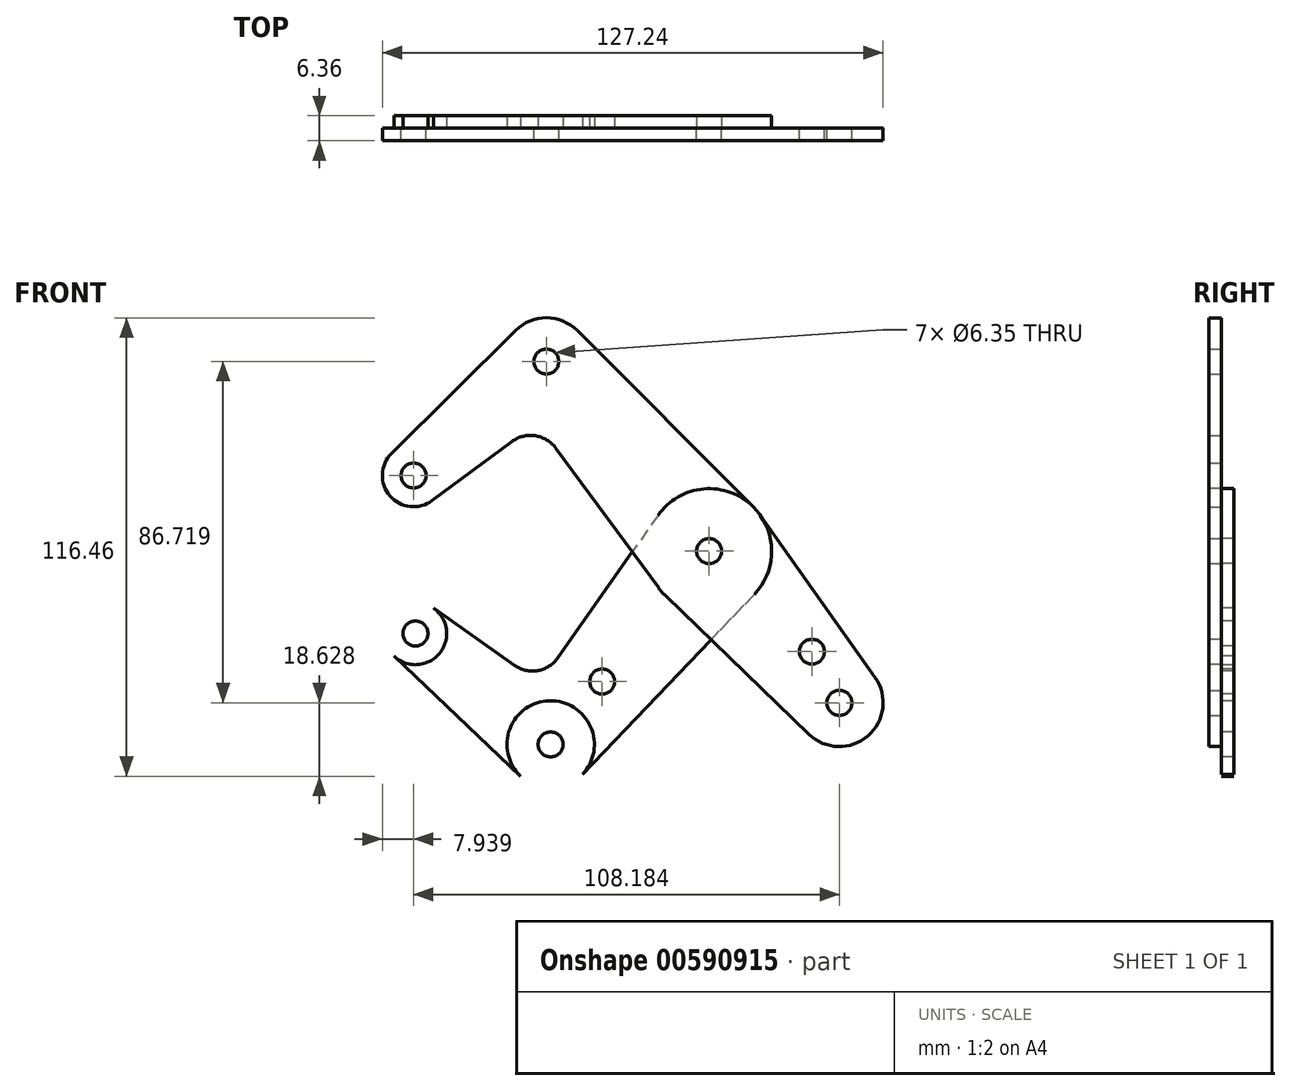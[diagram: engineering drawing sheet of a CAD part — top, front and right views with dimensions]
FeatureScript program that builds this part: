
annotation { "Feature Type Name" : "Feature", "Feature Type Description" : "" }
export const myFeature = defineFeature(function(context is Context, id is Id, definition is map)
    precondition{}
    {
        {
            var Q0;
            Q0=qCreatedBy(makeId("Front.planeOp"),FACE);
            var sketch = newSketch(context, id + "F0", { "sketchPlane" : qUnion([Q0])});
            skCircle(sketch, "E0", {"center": v(0, 0) * mm, "radius": 15.88 * mm});
            skCircle(sketch, "E1", {"center": v(-41.37, 48.18) * mm, "radius": 11.11 * mm});
            skCircle(sketch, "E2", {"center": v(-75.1, 19.22) * mm, "radius": 7.94 * mm});
            skCircle(sketch, "E3", {"center": v(33.1, -38.54) * mm, "radius": 11.11 * mm});
            skCircle(sketch, "E4", {"center": v(26.11, -25.54) * mm, "radius": 3.18 * mm});
            skCircle(sketch, "E5", {"center": v(-75.1, 19.22) * mm, "radius": 3.18 * mm});
            skCircle(sketch, "E6", {"center": v(-41.37, 48.18) * mm, "radius": 3.18 * mm});
            skCircle(sketch, "E7", {"center": v(0, 0) * mm, "radius": 3.98 * mm});
            skCircle(sketch, "E8", {"center": v(33.1, -38.54) * mm, "radius": 3.18 * mm});
            skLineSegment(sketch, "E9", {"start": v(-41.37, 48.18) * mm, "end": v(-75.1, 19.22) * mm, "construction": true});
            skCircle(sketch, "E10", {"center": v(0, 0) * mm, "radius": 3.18 * mm});
            skLineSegment(sketch, "E11", {"start": v(12.96, 9.17) * mm, "end": v(42.17, -32.12) * mm});
            skLineSegment(sketch, "E12", {"start": v(-80.68, 24.86) * mm, "end": v(-49.19, 56.07) * mm});
            skLineSegment(sketch, "E13", {"start": v(25.38, -46.54) * mm, "end": v(-11.02, -11.43) * mm});
            skLineSegment(sketch, "E14", {"start": v(-33.5, 56.03) * mm, "end": v(11.23, 11.22) * mm});
            skLineSegment(sketch, "E15", {"start": v(-12.79, -9.4) * mm, "end": v(-38.98, 26.18) * mm});
            skLineSegment(sketch, "E16", {"start": v(-70.36, 12.84) * mm, "end": v(-50.12, 27.86) * mm});
            skArc(sketch, "E17.filletArc", {"start": v(-38.98, 26.18) * mm, "mid": v(-44.2, 29.33) * mm, "end": v(-50.12, 27.86) * mm});
            skCircle(sketch, "E18.MirrorC", {"center": v(-40.26, -49.1) * mm, "radius": 3.18 * mm});
            skCircle(sketch, "E19.MirrorC", {"center": v(-74.63, -20.92) * mm, "radius": 3.18 * mm});
            skCircle(sketch, "E20.MirrorC", {"center": v(-74.63, -20.92) * mm, "radius": 7.94 * mm});
            skLineSegment(sketch, "E21.MirrorCS", {"start": v(-32.22, -56.77) * mm, "end": v(11.49, -10.96) * mm});
            skCircle(sketch, "E22.MirrorC", {"center": v(-40.26, -49.1) * mm, "radius": 11.11 * mm});
            skLineSegment(sketch, "E23.MirrorCS", {"start": v(-40.26, -49.1) * mm, "end": v(-74.63, -20.92) * mm, "construction": true});
            skLineSegment(sketch, "E24.MirrorCS", {"start": v(-70.05, -14.44) * mm, "end": v(-49.47, -28.99) * mm});
            skLineSegment(sketch, "E25.MirrorCS", {"start": v(-80.1, -26.68) * mm, "end": v(-47.9, -57.17) * mm});
            skLineSegment(sketch, "E26", {"start": v(-13, 9.12) * mm, "end": v(-38.37, -27.06) * mm});
            skArc(sketch, "E27.filletArc", {"start": v(-49.47, -28.99) * mm, "mid": v(-43.52, -30.33) * mm, "end": v(-38.37, -27.06) * mm});
            skLineSegment(sketch, "E28", {"start": v(0, 0) * mm, "end": v(-40.26, -49.1) * mm, "construction": true});
            skLineSegment(sketch, "E29", {"start": v(-40.26, -49.1) * mm, "end": v(-27.17, -33.14) * mm});
            skCircle(sketch, "E30", {"center": v(-27.17, -33.14) * mm, "radius": 3.18 * mm});
            skLineSegment(sketch, "E31", {"start": v(-41.37, 48.18) * mm, "end": v(0, 0) * mm, "construction": true});
            skLineSegment(sketch, "E32", {"start": v(0, 0) * mm, "end": v(33.1, -38.54) * mm, "construction": true});
            skSolve(sketch);
        }
        {
            var Q0;
            {var subQ0=sQuery(id+"F0.wireOp",EDGE,"E12");Q0=makeQuery(id+"F0.imprint","IMPRINT",FACE,{"disambiguationData":[TD([[makeQuery(id+"F0.imprint","IMPRINT",EDGE,{"derivedFrom":subQ0}),-1.0]])]});}
            var Q1;
            Q1=makeQuery(id+"F0.imprint","IMPRINT",FACE,{"disambiguationData":[TD([[makeQuery(id+"F0.imprint","IMPRINT",EDGE,{"derivedFrom":sQuery(id+"F0.wireOp",EDGE,"E6")}),-1.0]])]});
            var Q2;
            Q2=makeQuery(id+"F0.imprint","IMPRINT",FACE,{"disambiguationData":[TD([[makeQuery(id+"F0.imprint","IMPRINT",EDGE,{"derivedFrom":sQuery(id+"F0.wireOp",EDGE,"E4")}),-1.0]])]});
            var Q3;
            {var subQ0=sQuery(id+"F0.wireOp",EDGE,"E15");var subQ1=sQuery(id+"F0.wireOp",EDGE,"E0");var subQ2=makeQuery(id+"F0.imprint","INTERSECT",VERTEX,{"derivedFrom":[subQ1,subQ0]});Q3=makeQuery(id+"F0.imprint","IMPRINT",FACE,{"disambiguationData":[TD([[makeQuery(id+"F0.imprint","IMPRINT",EDGE,{"disambiguationData":[TD([[subQ2,1.0]])],"derivedFrom":subQ1}),-1.0]])]});}
            var Q4;
            {var subQ0=sQuery(id+"F0.wireOp",EDGE,"E13");var subQ1=sQuery(id+"F0.wireOp",EDGE,"E0");var subQ2=makeQuery(id+"F0.imprint","INTERSECT",VERTEX,{"derivedFrom":[subQ1,subQ0]});Q4=makeQuery(id+"F0.imprint","IMPRINT",FACE,{"disambiguationData":[TD([[makeQuery(id+"F0.imprint","IMPRINT",EDGE,{"disambiguationData":[TD([[subQ2,-1.0]])],"derivedFrom":subQ1}),-1.0]])]});}
            var Q5;
            Q5=makeQuery(id+"F0.imprint","IMPRINT",FACE,{"disambiguationData":[TD([[makeQuery(id+"F0.imprint","IMPRINT",EDGE,{"derivedFrom":sQuery(id+"F0.wireOp",EDGE,"E8")}),-1.0]])]});
            var Q6;
            Q6=makeQuery(id+"F0.imprint","IMPRINT",FACE,{"disambiguationData":[TD([[makeQuery(id+"F0.imprint","IMPRINT",EDGE,{"derivedFrom":sQuery(id+"F0.wireOp",EDGE,"E5")}),-1.0]])]});
            var Q7;
            Q7=makeQuery(id+"F0.imprint","IMPRINT",FACE,{"disambiguationData":[TD([[makeQuery(id+"F0.imprint","IMPRINT",EDGE,{"derivedFrom":sQuery(id+"F0.wireOp",EDGE,"E7")}),-1.0]])]});
            var Q8;
            Q8=makeQuery(id+"F0.imprint","IMPRINT",FACE,{"disambiguationData":[TD([[makeQuery(id+"F0.imprint","IMPRINT",EDGE,{"derivedFrom":sQuery(id+"F0.wireOp",EDGE,"E7")}),1.0]])]});
            extrude(context, id + "F1", {"entities" : qUnion([Q0, Q1, Q2, Q3, Q4, Q5, Q6, Q7, Q8]), "depth" : 3.17 * mm, "offsetDistance" : 25.4 * mm});
        }
        {
            var Q0;
            Q0=makeQuery(id+"F0.imprint","IMPRINT",FACE,{"disambiguationData":[TD([[makeQuery(id+"F0.imprint","IMPRINT",EDGE,{"derivedFrom":sQuery(id+"F0.wireOp",EDGE,"E19.MirrorC")}),1.0]])]});
            var Q1;
            Q1=makeQuery(id+"F0.imprint","IMPRINT",FACE,{"disambiguationData":[TD([[makeQuery(id+"F0.imprint","IMPRINT",EDGE,{"derivedFrom":sQuery(id+"F0.wireOp",EDGE,"E18.MirrorC")}),1.0]])]});
            var Q2;
            Q2=makeQuery(id+"F0.imprint","IMPRINT",FACE,{"disambiguationData":[TD([[makeQuery(id+"F0.imprint","IMPRINT",EDGE,{"derivedFrom":sQuery(id+"F0.wireOp",EDGE,"E7")}),-1.0]])]});
            var Q3;
            {var subQ11=sQuery(id+"F0.wireOp",EDGE,"E24.MirrorCS");Q3=makeQuery(id+"F0.imprint","IMPRINT",FACE,{"disambiguationData":[TD([[makeQuery(id+"F0.imprint","IMPRINT",EDGE,{"derivedFrom":subQ11}),-1.0]])]});}
            var Q4;
            {var subQ0=sQuery(id+"F0.wireOp",EDGE,"E13");var subQ1=sQuery(id+"F0.wireOp",EDGE,"E0");var subQ2=makeQuery(id+"F0.imprint","INTERSECT",VERTEX,{"derivedFrom":[subQ1,subQ0]});Q4=makeQuery(id+"F0.imprint","IMPRINT",FACE,{"disambiguationData":[TD([[makeQuery(id+"F0.imprint","IMPRINT",EDGE,{"disambiguationData":[TD([[subQ2,-1.0]])],"derivedFrom":subQ1}),-1.0]])]});}
            var Q5;
            {var subQ0=sQuery(id+"F0.wireOp",EDGE,"E15");var subQ1=sQuery(id+"F0.wireOp",EDGE,"E0");var subQ2=makeQuery(id+"F0.imprint","INTERSECT",VERTEX,{"derivedFrom":[subQ1,subQ0]});Q5=makeQuery(id+"F0.imprint","IMPRINT",FACE,{"disambiguationData":[TD([[makeQuery(id+"F0.imprint","IMPRINT",EDGE,{"disambiguationData":[TD([[subQ2,1.0]])],"derivedFrom":subQ1}),-1.0]])]});}
            var Q6;
            Q6=makeQuery(id+"F0.imprint","IMPRINT",FACE,{"disambiguationData":[TD([[makeQuery(id+"F0.imprint","IMPRINT",EDGE,{"derivedFrom":sQuery(id+"F0.wireOp",EDGE,"E7")}),1.0]])]});
            extrude(context, id + "F2", {"entities" : qUnion([Q0, Q1, Q2, Q3, Q4, Q5, Q6]), "oppositeDirection" : true, "depth" : 3.17 * mm, "offsetDistance" : 25.4 * mm});
        }
    });
